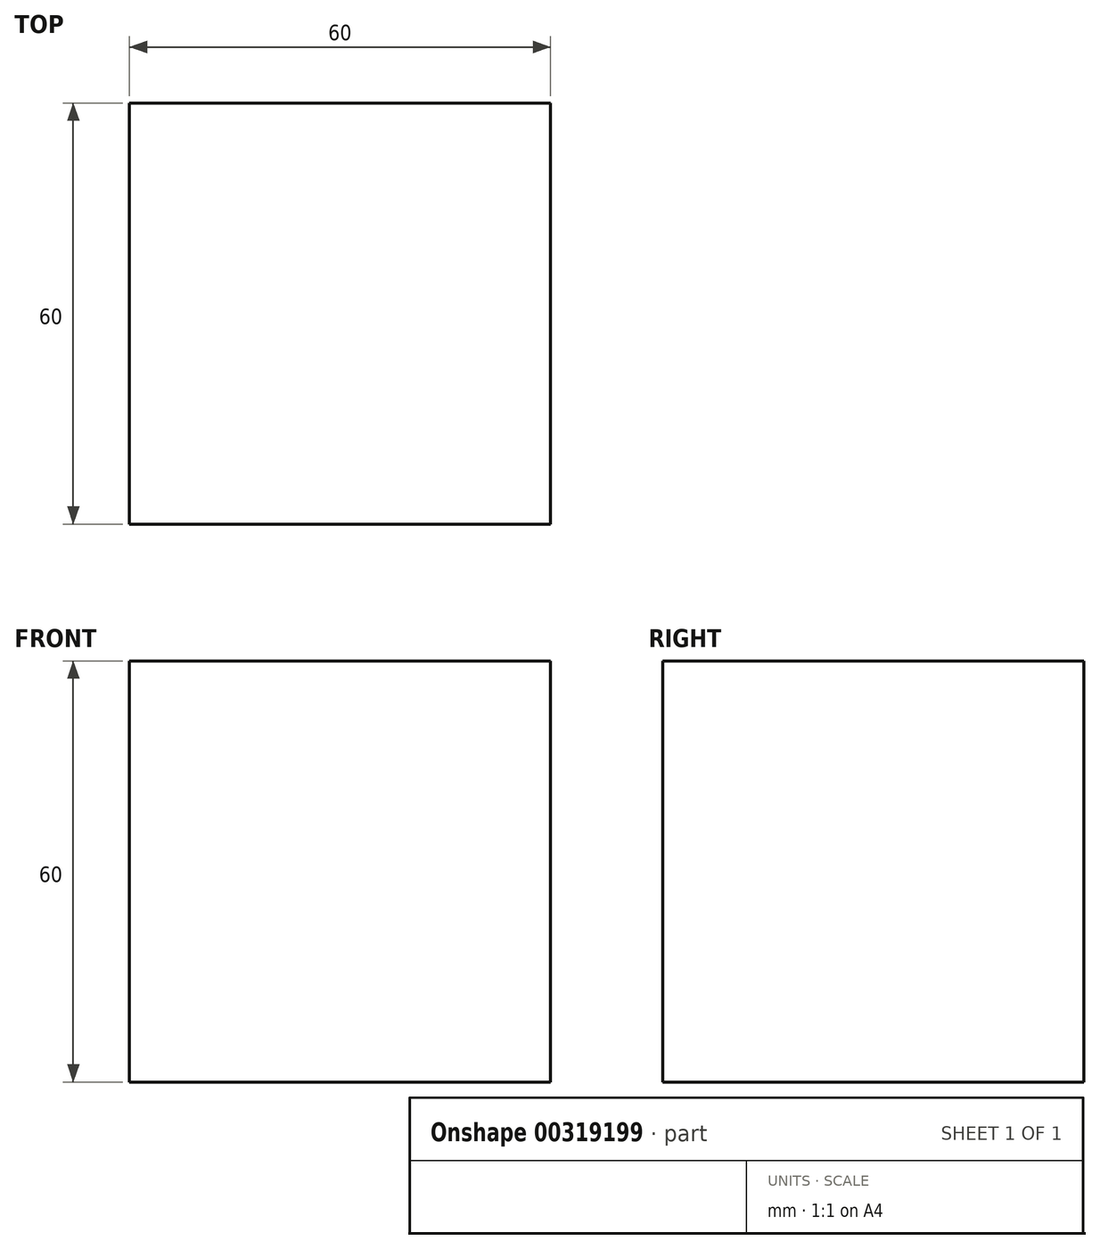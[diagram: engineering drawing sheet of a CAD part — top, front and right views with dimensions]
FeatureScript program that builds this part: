
annotation { "Feature Type Name" : "Feature", "Feature Type Description" : "" }
export const myFeature = defineFeature(function(context is Context, id is Id, definition is map)
    precondition{}
    {
        {
            var Q0;
            Q0=qCreatedBy(makeId("Front.planeOp"),FACE);
            var sketch = newSketch(context, id + "F0", { "sketchPlane" : qUnion([Q0])});
            skLineSegment(sketch, "E0.bottom", {"start": v(0, 0) * mm, "end": v(-60, 0) * mm});
            skLineSegment(sketch, "E0.top", {"start": v(0, -60) * mm, "end": v(-60, -60) * mm});
            skLineSegment(sketch, "E0.left", {"start": v(0, 0) * mm, "end": v(0, -60) * mm});
            skLineSegment(sketch, "E0.right", {"start": v(-60, 0) * mm, "end": v(-60, -60) * mm});
            skSolve(sketch);
        }
        {
            var Q0;
            Q0 = qSketchRegion(id + "F0", true);
            extrude(context, id + "F1", {"entities" : qUnion([Q0]), "depth" : 60 * mm});
        }
    });
